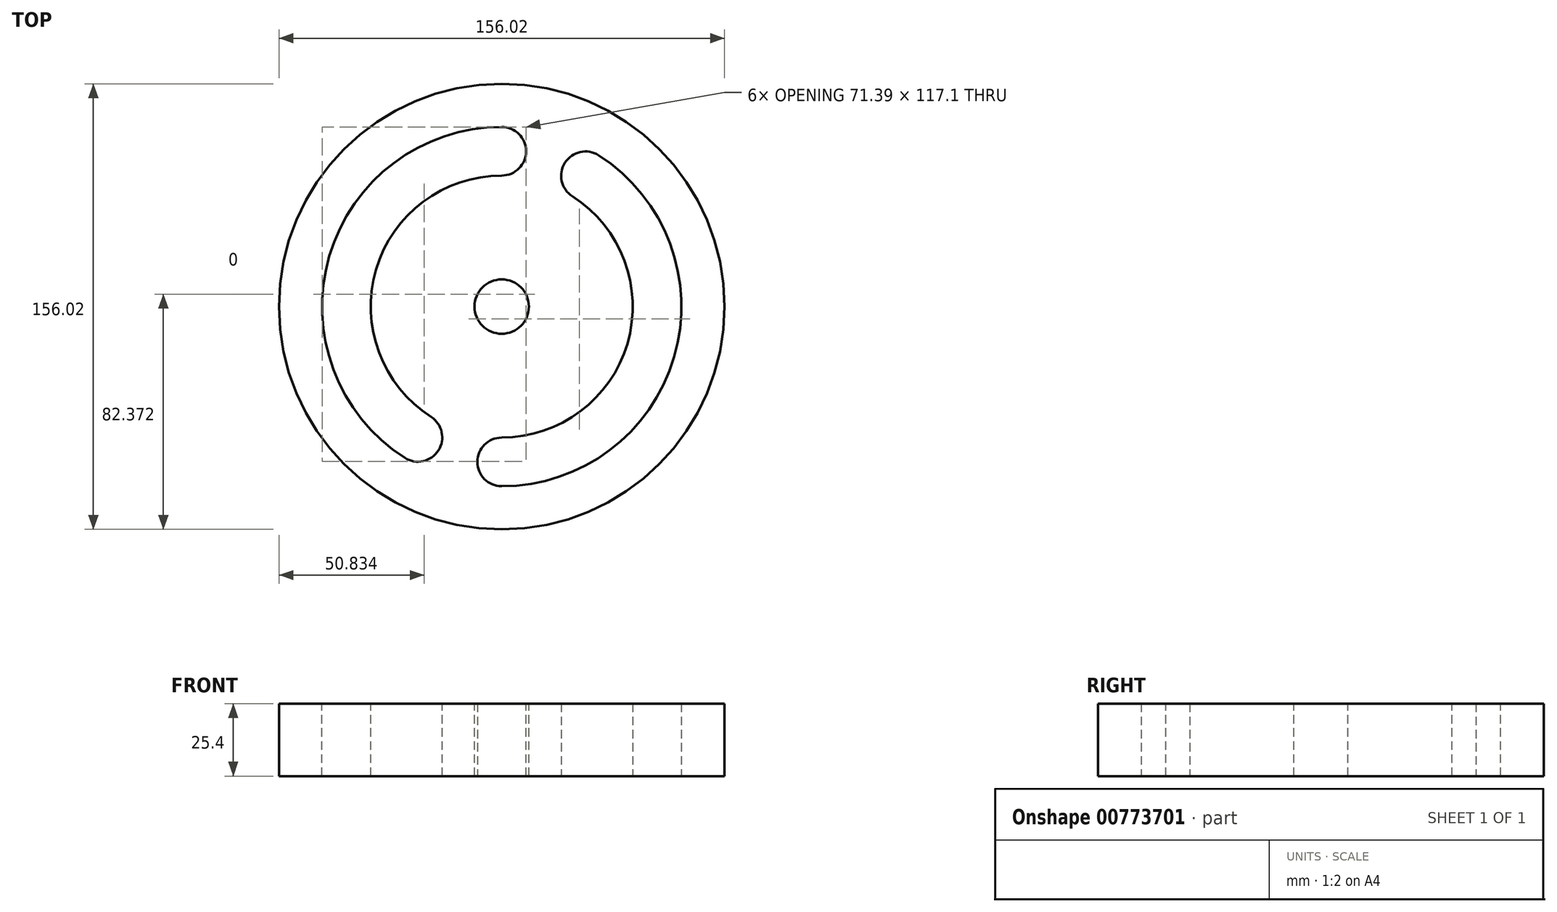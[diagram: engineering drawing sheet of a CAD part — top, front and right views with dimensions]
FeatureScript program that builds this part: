
annotation { "Feature Type Name" : "Feature", "Feature Type Description" : "" }
export const myFeature = defineFeature(function(context is Context, id is Id, definition is map)
    precondition{}
    {
        {
            var Q0;
            Q0=qCreatedBy(makeId("Top.planeOp"),FACE);
            var sketch = newSketch(context, id + "F0", { "sketchPlane" : qUnion([Q0])});
            skCircle(sketch, "E0", {"center": v(0, 0) * mm, "radius": 78.01 * mm});
            skSolve(sketch);
        }
        {
            var Q0;
            Q0 = qSketchRegion(id + "F0", true);
            extrude(context, id + "F1", {"entities" : qUnion([Q0]), "depth" : 25.4 * mm, "offsetDistance" : 25.4 * mm});
        }
        {
            var Q0;
            Q0=makeQuery(id+"F1.opExtrude","CAP_FACE",FACE,{"disambiguationData":[OSD([sQuery(id+"F0.wireOp",EDGE,"E0")])],"isStart":false});
            var sketch = newSketch(context, id + "F2", { "sketchPlane" : qUnion([Q0])});
            skCircle(sketch, "E1", {"center": v(0, 0) * mm, "radius": 9.51 * mm});
            skSolve(sketch);
        }
        {
            var Q0;
            Q0 = qSketchRegion(id + "F2", true);
            extrude(context, id + "F3", {"entities" : qUnion([Q0]), "operationType" : NewBodyOperationType.REMOVE, "endBound" : BoundingType.THROUGH_ALL, "oppositeDirection" : true, "depth" : 25.4 * mm, "offsetDistance" : 25.4 * mm});
        }
        {
            var Q0;
            Q0=makeQuery(id+"F1.opExtrude","CAP_FACE",FACE,{"disambiguationData":[OSD([sQuery(id+"F0.wireOp",EDGE,"E0")])],"isStart":true});
            var sketch = newSketch(context, id + "F4", { "sketchPlane" : qUnion([Q0])});
            skLineSegment(sketch, "E2", {"start": v(0, 27.03) * mm, "end": v(0, 27.8) * mm});
            skArc(sketch, "E3", {"start": v(0, 62.91) * mm, "mid": v(-8.52, 54.4) * mm, "end": v(0, 45.88) * mm});
            skArc(sketch, "E4", {"start": v(24.74, -38.63) * mm, "mid": v(44.03, 12.9) * mm, "end": v(0, 45.88) * mm});
            skArc(sketch, "E5", {"start": v(33.93, -52.98) * mm, "mid": v(60.38, 17.68) * mm, "end": v(0, 62.91) * mm});
            skLineSegment(sketch, "E6", {"start": v(0, 27.03) * mm, "end": v(-0.23, 27.22) * mm, "construction": true});
            skArc(sketch, "E7", {"start": v(24.74, -38.63) * mm, "mid": v(22.16, -50.4) * mm, "end": v(33.93, -52.98) * mm});
            skPoint(sketch, "E8.orphan", {"position": v(62.91, 0) * mm});
            skPoint(sketch, "E9.end.orphan", {"position": v(31.46, 0) * mm});
            skSolve(sketch);
        }
        {
            var Q0;
            Q0 = qSketchRegion(id + "F4", true);
            extrude(context, id + "F5", {"entities" : qUnion([Q0]), "operationType" : NewBodyOperationType.REMOVE, "endBound" : BoundingType.THROUGH_ALL, "oppositeDirection" : true, "depth" : 25.4 * mm, "offsetDistance" : 25.4 * mm});
        }
        {
            var Q0;
            Q0=makeQuery(id+"F1.opExtrude","CAP_FACE",FACE,{"disambiguationData":[OSD([sQuery(id+"F0.wireOp",EDGE,"E0")])],"isStart":false});
            var sketch = newSketch(context, id + "F6", { "sketchPlane" : qUnion([Q0])});
            skArc(sketch, "E10", {"start": v(0, 45.88) * mm, "mid": v(-44.03, 12.9) * mm, "end": v(-24.74, -38.63) * mm});
            skArc(sketch, "E11", {"start": v(0, 62.91) * mm, "mid": v(-60.38, 17.68) * mm, "end": v(-33.93, -52.98) * mm});
            skArc(sketch, "E12", {"start": v(-33.93, -52.98) * mm, "mid": v(-22.16, -50.4) * mm, "end": v(-24.74, -38.63) * mm});
            skArc(sketch, "E13", {"start": v(0, 45.88) * mm, "mid": v(8.52, 54.4) * mm, "end": v(0, 62.91) * mm});
            skPoint(sketch, "E14.start.orphan", {"position": v(29.34, 45.8) * mm});
            skSolve(sketch);
        }
        {
            var Q0;
            Q0 = qSketchRegion(id + "F6", true);
            extrude(context, id + "F7", {"entities" : qUnion([Q0]), "operationType" : NewBodyOperationType.REMOVE, "endBound" : BoundingType.THROUGH_ALL, "oppositeDirection" : true, "depth" : 25.4 * mm, "offsetDistance" : 25.4 * mm});
        }
    });
